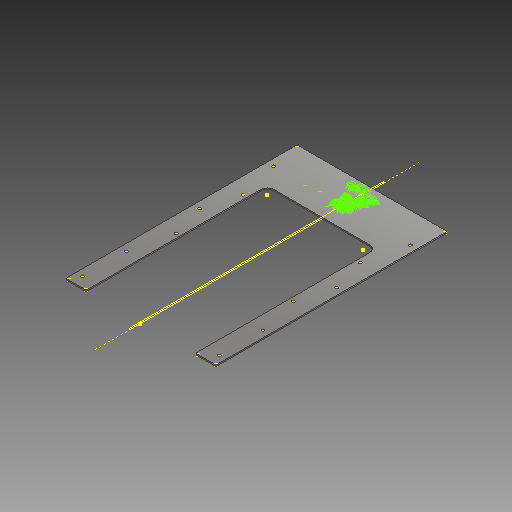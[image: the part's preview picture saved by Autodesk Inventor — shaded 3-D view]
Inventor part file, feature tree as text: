
AUTODESK INVENTOR PART (.ipt)
format: ipt  version: 2018 (Build 220112000, 112)  size: 396,288 bytes
history: native  units: mm
features: other x8, sketch x6, extrude x4, reference x3, fillet x2, projected_geometry x2, plane x1
ambient origin geometry x8: Origin, YZ Plane, XZ Plane, XY Plane, X Axis, Y Axis, Z Axis, Center Point
bodies: Volumenkörper1 (feature_tree)
feature tree (26):
  other  "Fläche1"
  fillet  "Rundung1"  Radius=81.5mm
  extrude  "Extrusion3"  Depth=270.0mm
  plane  "Arbeitsebene1"
  extrude  "Extrusion4"  Depth=345.0mm
  fillet  "Rundung2"  [1 undecoded]
  extrude  "Extrusion5"  Depth=2.0mm
  extrude  "Extrusion6"  Depth=6.0mm
  sketch  "Skizze8"  dims[d26=6.0mm d27=140.0mm d30=4.3mm d31=4.3mm d32=6.0mm d33=6.0mm d34=100.0mm d35=100.0mm d36=10.0mm d37=0.0mm d38=223.999834mm d39=345.0mm d40=10.0mm d41=0.0mm d42=2.0mm d43=10.0mm d44=0.0mm d45=10.0mm d46=4.3mm d47=4.3mm d48=10.0mm d49=15.0mm d50=10.0mm d51=0.0mm]
  sketch  "Skizze1"  dims[d1=81.5mm d3=270.0mm]
  reference  "Referenz1"
  reference  "Referenz2"
  reference  "Referenz3"
  other  "Grobblech1"
  sketch  "Skizze3"  dims[d4=10.0mm d6=345.0mm d7=0.0mm]
  projected_geometry  "Projizierte Kontur1"
  sketch  "Skizze4"  dims[d8=2.0mm d9=2.0mm]
  sketch  "Skizze6"  dims[d23=140.0mm d24=6.0mm]
  sketch  "Skizze7"  dims[d25=4.3mm]
  projected_geometry  "Projizierte Kontur2"
  other  "Bild1"
  other  "<userpath>\AppData\Local\Autodesk\Autodesk Sync\Cloud\jr9343s\Beefer_Montiert.iam"
  other  "Beefer_Montiert.iam"
  other  "Boden:1"
  parser-record x1  (decoder bookkeeping rows leaked as tree rows — omitted from the tree; the rows remain in map.json)
  other  "Definition1"
note: 1 required parameter value undecoded (feature->parameter linkage not recoverable at this tier; creation-order binding heuristic only, values carry confidence <= 0.55)
note: 1 file-system path scrubbed to <path> (originals preserved in map.json)
